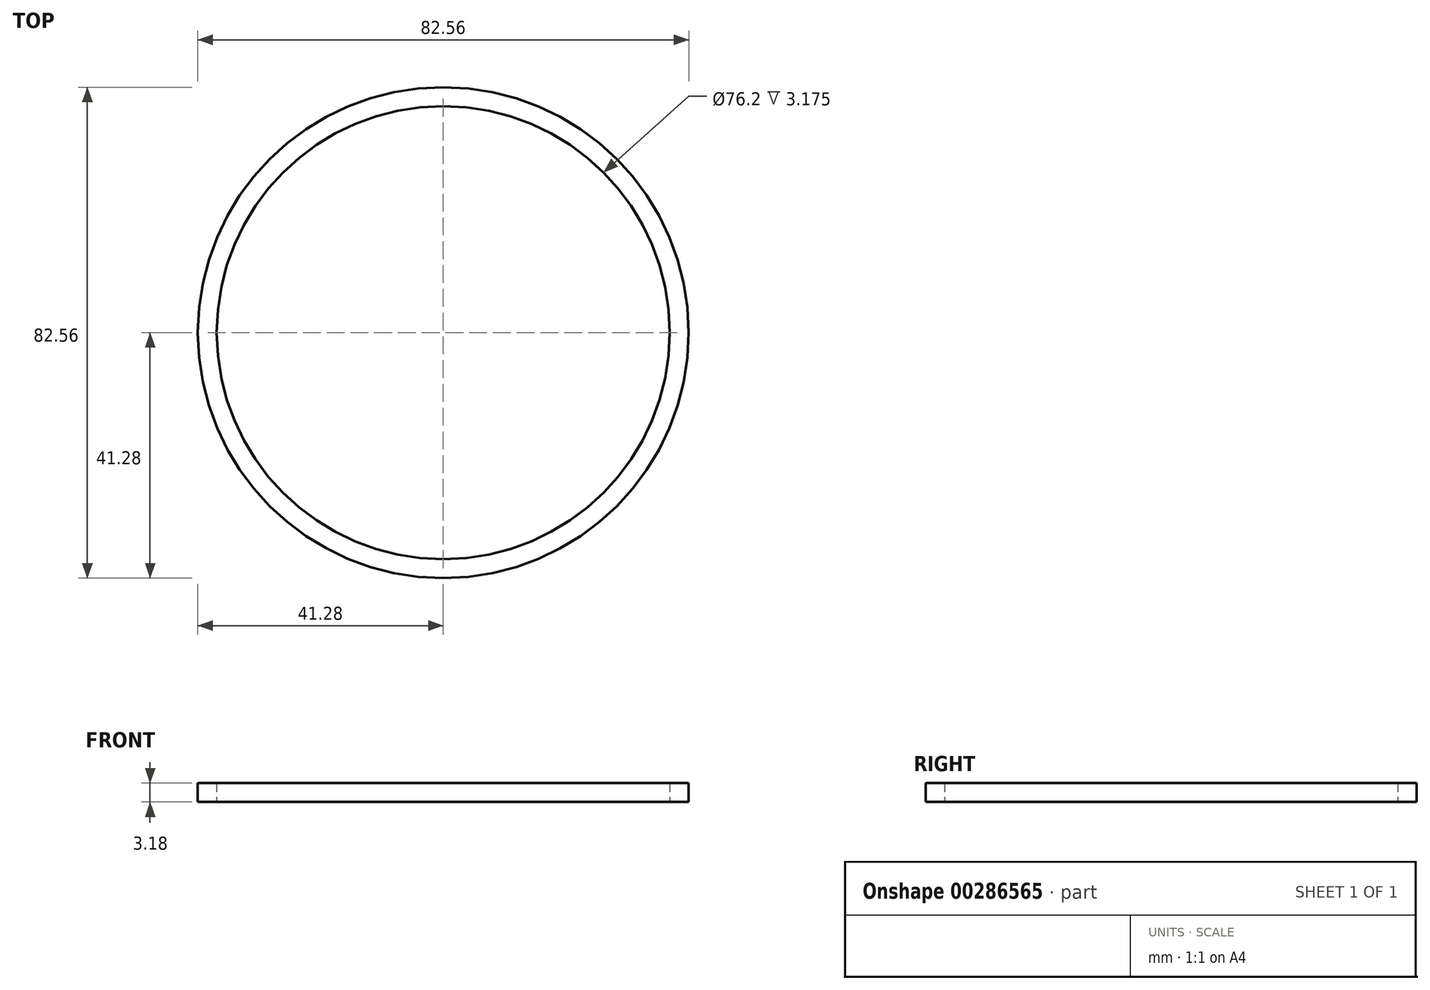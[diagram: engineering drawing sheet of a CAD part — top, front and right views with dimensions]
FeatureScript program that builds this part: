
annotation { "Feature Type Name" : "Feature", "Feature Type Description" : "" }
export const myFeature = defineFeature(function(context is Context, id is Id, definition is map)
    precondition{}
    {
        {
            var Q0;
            Q0=qCreatedBy(makeId("Top.planeOp"),FACE);
            var sketch = newSketch(context, id + "F0", { "sketchPlane" : qUnion([Q0])});
            skCircle(sketch, "E0", {"center": v(0, 0) * mm, "radius": 41.28 * mm});
            skCircle(sketch, "E1", {"center": v(0, 0) * mm, "radius": 38.1 * mm});
            skSolve(sketch);
        }
        {
            var Q0;
            Q0=makeQuery(id+"F0.imprint","IMPRINT",FACE,{"disambiguationData":[TD([[makeQuery(id+"F0.imprint","IMPRINT",EDGE,{"derivedFrom":sQuery(id+"F0.wireOp",EDGE,"E0")}),1.0]])]});
            extrude(context, id + "F1", {"entities" : qUnion([Q0]), "depth" : 3.17 * mm});
        }
    });
